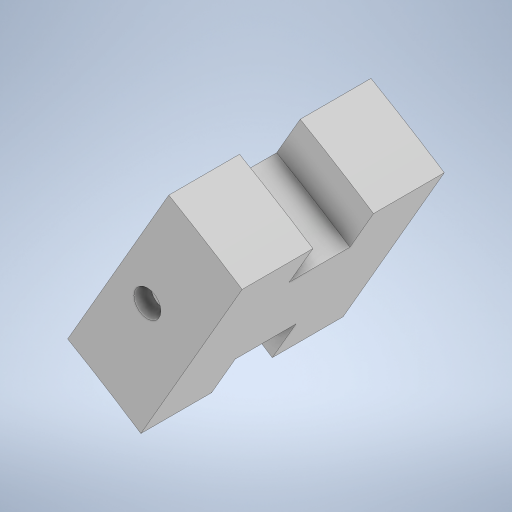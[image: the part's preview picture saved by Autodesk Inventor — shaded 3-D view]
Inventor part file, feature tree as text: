
AUTODESK INVENTOR PART (.ipt)
format: ipt  version: 2023 (Build 270158000, 158)  size: 330,752 bytes
history: native  units: mm
features: sketch x7, extrude x5, sweep x1
ambient origin geometry x8: Origin, YZ Plane, XZ Plane, XY Plane, X Axis, Y Axis, Z Axis, Center Point
bodies: Body1 (feature_tree)
feature tree (13):
  sweep  "Sweep2"
  extrude  "Extrusion3"  Depth=7.0mm
  extrude  "Extrusion5"  Depth=30.0mm
  extrude  "Extrusion6"  Depth=8.0mm
  extrude  "Extrusion7"  TaperAngle=60.0deg  [1 undecoded]
  extrude  "Extrusion8"  TaperAngle=0.0deg  [1 undecoded]
  sketch  "Sketch2"  dims[d5=100.0mm d18=9.0mm]
  sketch  "Sketch6"  dims[d19=7.0mm d21=16.0mm]
  sketch  "Sketch7"  dims[d22=30.0mm d23=15.0mm]
  sketch  "Sketch9"  dims[d24=4.5mm d25=8.0mm]
  sketch  "Sketch10"  dims[d41=220.0mm d42=60.0deg]
  sketch  "Sketch11"  dims[d43=220.0mm d44=0.0mm]
  sketch  "Sketch12"  dims[d45=0.0mm d46=0.0mm d47=2.5mm d48=2.5mm d49=2.5mm d50=2.5mm d51=2.5mm d52=2.5mm d53=2.5mm d54=2.5mm d55=2.5mm d56=10.0mm d57=0.0mm d63=4.0mm d65=5.0mm d66=15.0mm d67=0.0mm d68=0.0mm d69=3.0mm d70=3.0mm d71=3.0mm d72=3.0mm d73=3.0mm d74=3.0mm d75=3.0mm d76=3.0mm d77=10.0mm d78=0.0mm d79=4.0mm d80=5.0mm d81=15.0mm d82=0.0mm d83=0.0mm d85=239.167981mm d86=37.057395mm d87=18.642371mm d88=0.0mm d89=0.0mm d90=148.207407mm d91=115.0mm d92=181.651065mm]
note: 2 required parameter values undecoded (feature->parameter linkage not recoverable at this tier; creation-order binding heuristic only, values carry confidence <= 0.55)
